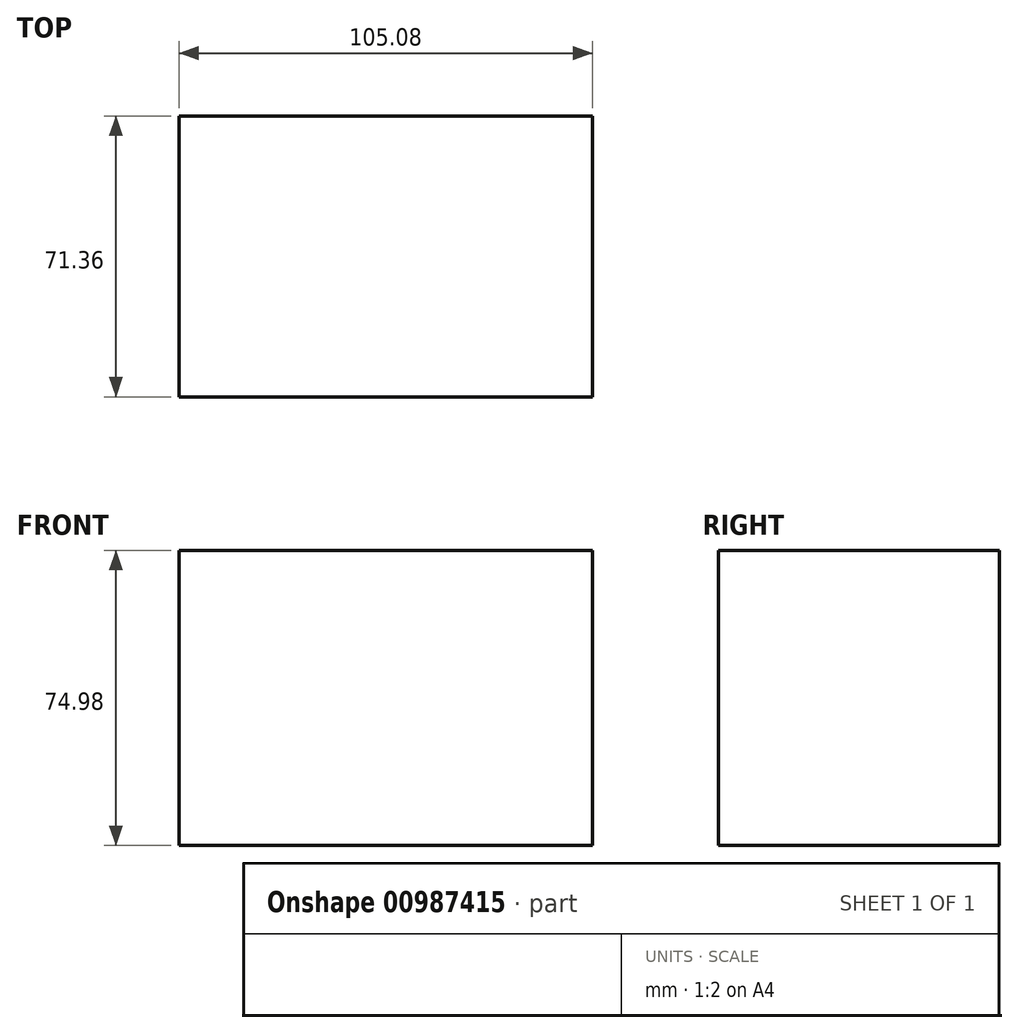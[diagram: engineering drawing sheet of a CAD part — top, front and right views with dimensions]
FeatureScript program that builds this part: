
annotation { "Feature Type Name" : "Feature", "Feature Type Description" : "" }
export const myFeature = defineFeature(function(context is Context, id is Id, definition is map)
    precondition{}
    {
        {
            var Q0;
            Q0=qCreatedBy(makeId("Front.planeOp"),FACE);
            var sketch = newSketch(context, id + "F0", { "sketchPlane" : qUnion([Q0])});
            skLineSegment(sketch, "E0.bottom", {"start": v(52.54, 67.57) * mm, "end": v(-52.54, 67.57) * mm});
            skLineSegment(sketch, "E0.top", {"start": v(52.54, -7.4) * mm, "end": v(-52.54, -7.4) * mm});
            skLineSegment(sketch, "E0.left", {"start": v(52.54, 67.57) * mm, "end": v(52.54, -7.4) * mm});
            skLineSegment(sketch, "E0.right", {"start": v(-52.54, 67.57) * mm, "end": v(-52.54, -7.4) * mm});
            skPoint(sketch, "E0.middle", {"position": v(0, 30.08) * mm});
            skSolve(sketch);
        }
        {
            var Q0;
            Q0 = qSketchRegion(id + "F0", true);
            extrude(context, id + "F1", {"entities" : qUnion([Q0]), "endBound" : BoundingType.SYMMETRIC, "depth" : 71.37 * mm, "offsetDistance" : 25.4 * mm});
        }
    });
